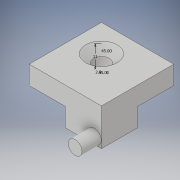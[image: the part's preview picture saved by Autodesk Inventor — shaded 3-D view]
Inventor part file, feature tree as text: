
AUTODESK INVENTOR PART (.ipt)
format: ipt  version: 2019 (Build 230136000, 136)  size: 148,992 bytes
history: native  units: mm
features: sketch x5, extrude x3, hole x1
ambient origin geometry x8: Origin, YZ Plane, XZ Plane, XY Plane, X Axis, Y Axis, Z Axis, Center Point
bodies: Solid1 (feature_tree)
feature tree (9):
  extrude  "Base"  Depth=25.4mm
  extrude  "Back extrusion"  Depth=6.35mm
  extrude  "Extrusion3"  Depth=6.5mm TaperAngle=0.0deg
  sketch  "Sketch6"  dims[d10=5.0mm d11=5.0mm]
  hole  "Hole1"  [1 undecoded]
  sketch  "Sketch2"  dims[d2=25.4mm d3=25.4mm]
  sketch  "Sketch3"  dims[d4=6.5mm d5=0.0mm d6=6.35mm]
  sketch  "Sketch5"  dims[d7=12.7mm d8=6.5mm d9=0.0mm]
  sketch  "Sketch7"  dims[d12=4.85mm d13=6.75mm d14=0.0mm d15=11.0mm d16=45.0deg d17=2.5mm d18=45.0deg d19=8.0mm d20=45.0deg d21=5.5mm d22=45.0deg d23=5.5mm d24=6.0mm d25=11.0mm d26=2.0mm d27=90.0deg d28=2.5mm d29=0.0mm]
note: 1 required parameter value undecoded (feature->parameter linkage not recoverable at this tier; creation-order binding heuristic only, values carry confidence <= 0.55)
